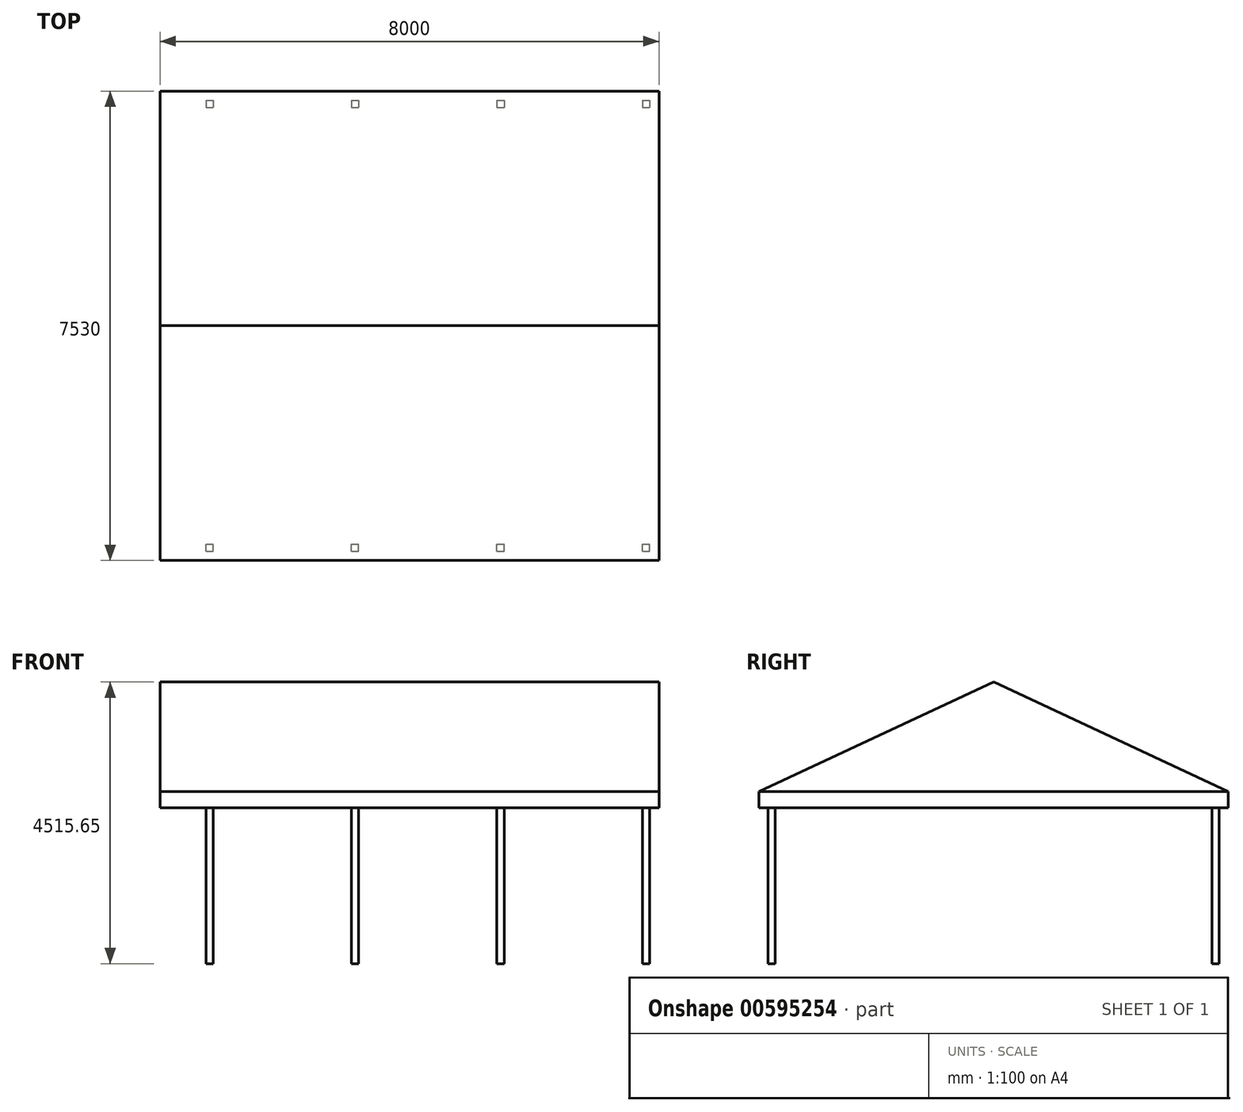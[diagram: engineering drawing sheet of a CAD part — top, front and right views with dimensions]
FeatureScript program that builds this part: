
annotation { "Feature Type Name" : "Feature", "Feature Type Description" : "" }
export const myFeature = defineFeature(function(context is Context, id is Id, definition is map)
    precondition{}
    {
        {
            var Q0;
            Q0=qCreatedBy(makeId("Top.planeOp"),FACE);
            var sketch = newSketch(context, id + "F0", { "sketchPlane" : qUnion([Q0])});
            skLineSegment(sketch, "E0.bottom", {"start": v(-57.5, 115) * mm, "end": v(57.5, 115) * mm});
            skLineSegment(sketch, "E0.top", {"start": v(-57.5, 0) * mm, "end": v(57.5, 0) * mm});
            skLineSegment(sketch, "E0.left", {"start": v(-57.5, 115) * mm, "end": v(-57.5, 0) * mm});
            skLineSegment(sketch, "E0.right", {"start": v(57.5, 115) * mm, "end": v(57.5, 0) * mm});
            skLineSegment(sketch, "E1.bottom", {"start": v(-2390.8, 115) * mm, "end": v(-2275.8, 115) * mm});
            skLineSegment(sketch, "E1.top", {"start": v(-2390.8, 0) * mm, "end": v(-2275.8, 0) * mm});
            skLineSegment(sketch, "E1.left", {"start": v(-2390.8, 115) * mm, "end": v(-2390.8, 0) * mm});
            skLineSegment(sketch, "E1.right", {"start": v(-2275.8, 115) * mm, "end": v(-2275.8, 0) * mm});
            skLineSegment(sketch, "E2.bottom", {"start": v(-4724.2, 115) * mm, "end": v(-4609.2, 115) * mm});
            skLineSegment(sketch, "E2.top", {"start": v(-4724.2, 0) * mm, "end": v(-4609.2, 0) * mm});
            skLineSegment(sketch, "E2.left", {"start": v(-4724.2, 115) * mm, "end": v(-4724.2, 0) * mm});
            skLineSegment(sketch, "E2.right", {"start": v(-4609.2, 115) * mm, "end": v(-4609.2, 0) * mm});
            skLineSegment(sketch, "E3.bottom", {"start": v(-7057.5, 115) * mm, "end": v(-6942.5, 115) * mm});
            skLineSegment(sketch, "E3.top", {"start": v(-7057.5, 0) * mm, "end": v(-6942.5, 0) * mm});
            skLineSegment(sketch, "E3.left", {"start": v(-7057.5, 115) * mm, "end": v(-7057.5, 0) * mm});
            skLineSegment(sketch, "E3.right", {"start": v(-6942.5, 115) * mm, "end": v(-6942.5, 0) * mm});
            skLineSegment(sketch, "E4", {"start": v(-8589.93, -3500) * mm, "end": v(2804.82, -3500) * mm, "construction": true});
            skLineSegment(sketch, "E5.MirrorCS", {"start": v(-4724.2, -7000) * mm, "end": v(-4609.2, -7000) * mm});
            skLineSegment(sketch, "E6.MirrorCS", {"start": v(-57.5, -7000) * mm, "end": v(57.5, -7000) * mm});
            skLineSegment(sketch, "E7.MirrorCS", {"start": v(-57.5, -7115) * mm, "end": v(57.5, -7115) * mm});
            skLineSegment(sketch, "E8.MirrorCS", {"start": v(-4724.2, -7115) * mm, "end": v(-4609.2, -7115) * mm});
            skLineSegment(sketch, "E9.MirrorCS", {"start": v(-4609.2, -7115) * mm, "end": v(-4609.2, -7000) * mm});
            skLineSegment(sketch, "E10.MirrorCS", {"start": v(57.5, -7115) * mm, "end": v(57.5, -7000) * mm});
            skLineSegment(sketch, "E11.MirrorCS", {"start": v(-57.5, -7115) * mm, "end": v(-57.5, -7000) * mm});
            skLineSegment(sketch, "E12.MirrorCS", {"start": v(-4724.2, -7115) * mm, "end": v(-4724.2, -7000) * mm});
            skLineSegment(sketch, "E13.MirrorCS", {"start": v(-2390.8, -7000) * mm, "end": v(-2275.8, -7000) * mm});
            skLineSegment(sketch, "E14.MirrorCS", {"start": v(-7057.5, -7000) * mm, "end": v(-6942.5, -7000) * mm});
            skLineSegment(sketch, "E15.MirrorCS", {"start": v(-2275.8, -7115) * mm, "end": v(-2275.8, -7000) * mm});
            skLineSegment(sketch, "E16.MirrorCS", {"start": v(-2390.8, -7115) * mm, "end": v(-2390.8, -7000) * mm});
            skLineSegment(sketch, "E17.MirrorCS", {"start": v(-6942.5, -7115) * mm, "end": v(-6942.5, -7000) * mm});
            skLineSegment(sketch, "E18.MirrorCS", {"start": v(-7057.5, -7115) * mm, "end": v(-7057.5, -7000) * mm});
            skLineSegment(sketch, "E19.MirrorCS", {"start": v(-7057.5, -7115) * mm, "end": v(-6942.5, -7115) * mm});
            skLineSegment(sketch, "E20.MirrorCS", {"start": v(-2390.8, -7115) * mm, "end": v(-2275.8, -7115) * mm});
            skSolve(sketch);
        }
        {
            var Q0;
            Q0=qCreatedBy(makeId("Top.planeOp"),FACE);
            var sketch = newSketch(context, id + "F1", { "sketchPlane" : qUnion([Q0])});
            skLineSegment(sketch, "E21.bottom", {"start": v(207.5, 265) * mm, "end": v(-7792.5, 265) * mm});
            skLineSegment(sketch, "E21.top", {"start": v(207.5, -7265) * mm, "end": v(-7792.5, -7265) * mm});
            skLineSegment(sketch, "E21.left", {"start": v(207.5, 265) * mm, "end": v(207.5, -7265) * mm});
            skLineSegment(sketch, "E21.right", {"start": v(-7792.5, 265) * mm, "end": v(-7792.5, -7265) * mm});
            skSolve(sketch);
        }
        {
            var Q0;
            Q0 = qSketchRegion(id + "F0", true);
            extrude(context, id + "F2", {"entities" : qUnion([Q0]), "oppositeDirection" : true, "depth" : 2500 * mm, "offsetDistance" : 25 * mm});
        }
        {
            var Q0;
            Q0=qCreatedBy(makeId("Right.planeOp"),FACE);
            var sketch = newSketch(context, id + "F3", { "sketchPlane" : qUnion([Q0])});
            skLineSegment(sketch, "E22.bottom", {"start": v(-7265, 0) * mm, "end": v(265, 0) * mm});
            skLineSegment(sketch, "E22.top", {"start": v(-7265, 260) * mm, "end": v(265, 260) * mm});
            skLineSegment(sketch, "E22.left", {"start": v(-7265, 0) * mm, "end": v(-7265, 260) * mm});
            skLineSegment(sketch, "E22.right", {"start": v(265, 0) * mm, "end": v(265, 260) * mm});
            skLineSegment(sketch, "E23", {"start": v(-7265, 260) * mm, "end": v(-3500, 2015.65) * mm});
            skLineSegment(sketch, "E24", {"start": v(-3500, 2015.65) * mm, "end": v(265, 260) * mm});
            skSolve(sketch);
        }
        {
            var Q0;
            Q0 = qSketchRegion(id + "F1", true);
            extrude(context, id + "F4", {"entities" : qUnion([Q0]), "depth" : 260 * mm, "offsetDistance" : 25 * mm});
        }
        {
            var Q0;
            Q0 = qSketchRegion(id + "F3", true);
            var Q1;
            Q1=makeQuery(id+"F4.opExtrude","SWEPT_FACE",FACE,{"disambiguationData":[OSD([sQuery(id+"F1.wireOp",EDGE,"E21.left")])]});
            var Q2;
            Q2=makeQuery(id+"F4.opExtrude","SWEPT_FACE",FACE,{"disambiguationData":[OSD([sQuery(id+"F1.wireOp",EDGE,"E21.right")])]});
            extrude(context, id + "F5", {"entities" : qUnion([Q0]), "endBound" : BoundingType.UP_TO_SURFACE, "depth" : 25 * mm, "endBoundEntityFace" : qUnion([Q1]), "offsetDistance" : 25 * mm, "hasSecondDirection" : true, "secondDirectionBound" : SecondDirectionBoundingType.UP_TO_SURFACE, "secondDirectionOppositeDirection" : true, "secondDirectionDepth" : 25 * mm, "secondDirectionBoundEntityFace" : qUnion([Q2])});
        }
    });
